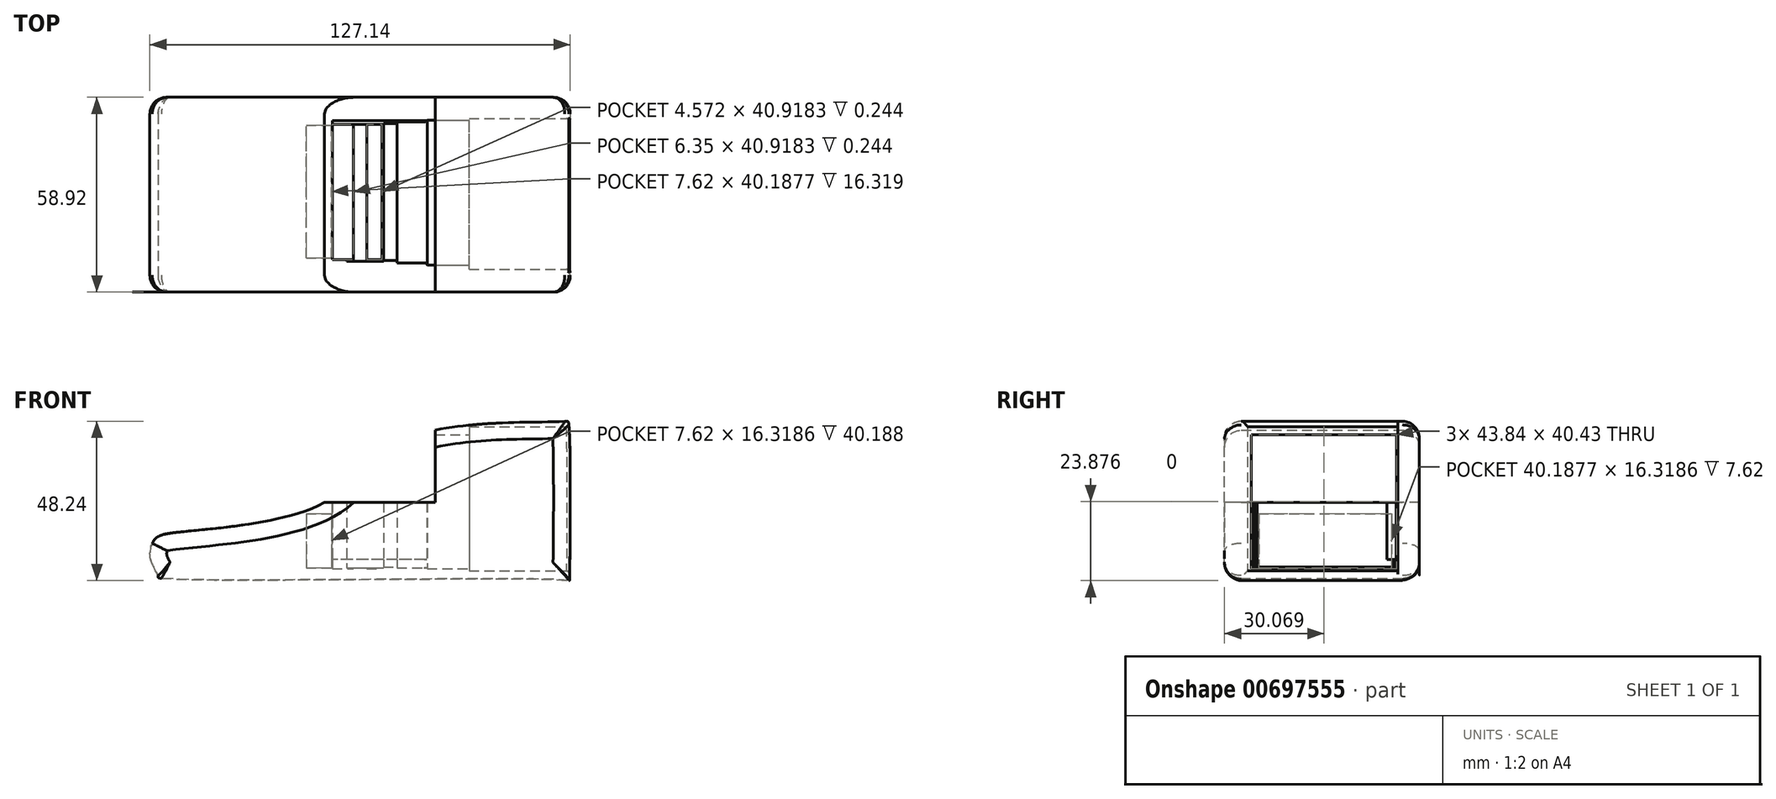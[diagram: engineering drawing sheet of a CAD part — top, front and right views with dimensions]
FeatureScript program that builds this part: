
annotation { "Feature Type Name" : "Feature", "Feature Type Description" : "" }
export const myFeature = defineFeature(function(context is Context, id is Id, definition is map)
    precondition{}
    {
        {
            var Q0;
            Q0=qCreatedBy(makeId("Front.planeOp"),FACE);
            var sketch = newSketch(context, id + "F0", { "sketchPlane" : qUnion([Q0])});
            skFitSpline(sketch, "E0", {"points": [v(-75, 0) * mm, v(-74, 5.82) * mm, v(-68.46, 8.09) * mm, v(-23.14, 16.9) * mm, v(3.56, 37.05) * mm, v(50.4, 41.83) * mm, v(51.4, 41.33) * mm, v(51.65, -6.27) * mm, v(51.4, -6.27) * mm, v(-72.5, -5.51) * mm, v(-72.74, -5) * mm, v(-75, 0) * mm]});
            skSolve(sketch);
        }
        {
            var Q0;
            Q0=makeQuery(id+"F0.imprint","IMPRINT",FACE,{"disambiguationData":[TD([[makeQuery(id+"F0.imprint","IMPRINT",EDGE,{"derivedFrom":sQuery(id+"F0.wireOp",EDGE,"E0")}),-1.0]])]});
            extrude(context, id + "F1", {"entities" : qUnion([Q0]), "endBound" : BoundingType.SYMMETRIC, "depth" : 58.93 * mm, "offsetDistance" : 25.4 * mm});
        }
        {
            var Q0;
            Q0=makeQuery(id+"F1.opExtrude","CAP_EDGE",EDGE,{"disambiguationData":[OSD([sQuery(id+"F0.wireOp",EDGE,"E0")])],"isStart":false});
            var Q1;
            Q1=makeQuery(id+"F1.opExtrude","CAP_EDGE",EDGE,{"disambiguationData":[OSD([sQuery(id+"F0.wireOp",EDGE,"E0")])],"isStart":true});
            fillet(context, id + "F2", {"entities" : qUnion([Q0, Q1]), "radius" : 5.08 * mm, "tangentPropagation" : true, "allowEdgeOverflow" : false});
        }
        {
            var Q0;
            Q0=qCreatedBy(makeId("Right.planeOp"),FACE);
            cPlane(context, id + "F3", {"entities" : qUnion([Q0]), "cplaneType" : CPlaneType.OFFSET, "offset" : 52.32 * mm, "width" : 152.4 * mm, "height" : 152.4 * mm});
        }
        {
            var Q0;
            Q0=qCreatedBy(id+"F3.planeOp",FACE);
            var sketch = newSketch(context, id + "F4", { "sketchPlane" : qUnion([Q0])});
            skLineSegment(sketch, "E1.bottom", {"start": v(-22.53, 40.19) * mm, "end": v(23.02, 40.19) * mm});
            skLineSegment(sketch, "E1.top", {"start": v(-22.53, -3.4) * mm, "end": v(23.02, -3.4) * mm});
            skLineSegment(sketch, "E1.left", {"start": v(-22.53, 40.19) * mm, "end": v(-22.53, -3.4) * mm});
            skLineSegment(sketch, "E1.right", {"start": v(23.02, 40.19) * mm, "end": v(23.02, -3.4) * mm});
            skSolve(sketch);
        }
        {
            var Q0;
            Q0=makeQuery(id+"F4.imprint","IMPRINT",FACE,{"disambiguationData":[TD([[makeQuery(id+"F4.imprint","IMPRINT",EDGE,{"derivedFrom":sQuery(id+"F4.wireOp",EDGE,"E1.bottom")}),-1.0]])]});
            extrude(context, id + "F5", {"entities" : qUnion([Q0]), "operationType" : NewBodyOperationType.REMOVE, "oppositeDirection" : true, "depth" : 30.99 * mm, "offsetDistance" : 25.4 * mm});
        }
        {
            var Q0;
            Q0=qCreatedBy(makeId("Right.planeOp"),FACE);
            cPlane(context, id + "F6", {"entities" : qUnion([Q0]), "cplaneType" : CPlaneType.OFFSET, "offset" : 21.34 * mm, "width" : 152.4 * mm, "height" : 152.4 * mm});
        }
        {
            var Q0;
            Q0=qCreatedBy(id+"F6.planeOp",FACE);
            var sketch = newSketch(context, id + "F7", { "sketchPlane" : qUnion([Q0])});
            skLineSegment(sketch, "E2.bottom", {"start": v(-21.31, 37.75) * mm, "end": v(22.53, 37.75) * mm});
            skLineSegment(sketch, "E2.top", {"start": v(-21.31, -2.68) * mm, "end": v(22.53, -2.68) * mm});
            skLineSegment(sketch, "E2.left", {"start": v(-21.31, 37.75) * mm, "end": v(-21.31, -2.68) * mm});
            skLineSegment(sketch, "E2.right", {"start": v(22.53, 37.75) * mm, "end": v(22.53, -2.68) * mm});
            skSolve(sketch);
        }
        {
            var Q0;
            Q0=makeQuery(id+"F7.imprint","IMPRINT",FACE,{"disambiguationData":[TD([[makeQuery(id+"F7.imprint","IMPRINT",EDGE,{"derivedFrom":sQuery(id+"F7.wireOp",EDGE,"E2.bottom")}),-1.0]])]});
            extrude(context, id + "F8", {"entities" : qUnion([Q0]), "operationType" : NewBodyOperationType.REMOVE, "oppositeDirection" : true, "depth" : 12.7 * mm, "offsetDistance" : 25.4 * mm});
        }
        {
            var Q0;
            Q0=qCreatedBy(makeId("Right.planeOp"),FACE);
            cPlane(context, id + "F9", {"entities" : qUnion([Q0]), "cplaneType" : CPlaneType.OFFSET, "offset" : 11.18 * mm, "width" : 152.4 * mm, "height" : 152.4 * mm});
        }
        {
            var Q0;
            Q0=qCreatedBy(id+"F9.planeOp",FACE);
            var sketch = newSketch(context, id + "F10", { "sketchPlane" : qUnion([Q0])});
            skLineSegment(sketch, "E3.bottom", {"start": v(-20.58, 34.59) * mm, "end": v(22.04, 34.59) * mm});
            skLineSegment(sketch, "E3.top", {"start": v(-20.58, -2.44) * mm, "end": v(22.04, -2.44) * mm});
            skLineSegment(sketch, "E3.left", {"start": v(-20.58, 34.59) * mm, "end": v(-20.58, -2.44) * mm});
            skLineSegment(sketch, "E3.right", {"start": v(22.04, 34.59) * mm, "end": v(22.04, -2.44) * mm});
            skSolve(sketch);
        }
        {
            var Q0;
            Q0=makeQuery(id+"F10.imprint","IMPRINT",FACE,{"disambiguationData":[TD([[makeQuery(id+"F10.imprint","IMPRINT",EDGE,{"derivedFrom":sQuery(id+"F10.wireOp",EDGE,"E3.bottom")}),-1.0]])]});
            extrude(context, id + "F11", {"entities" : qUnion([Q0]), "operationType" : NewBodyOperationType.REMOVE, "oppositeDirection" : true, "depth" : 11.68 * mm, "offsetDistance" : 25.4 * mm});
        }
        {
            var Q0;
            Q0=qCreatedBy(makeId("Right.planeOp"),FACE);
            var sketch = newSketch(context, id + "F12", { "sketchPlane" : qUnion([Q0])});
            skLineSegment(sketch, "E4.bottom", {"start": v(-19.85, 31.42) * mm, "end": v(21.56, 31.42) * mm});
            skLineSegment(sketch, "E4.top", {"start": v(-19.85, -2.2) * mm, "end": v(21.56, -2.2) * mm});
            skLineSegment(sketch, "E4.left", {"start": v(-19.85, 31.42) * mm, "end": v(-19.85, -2.2) * mm});
            skLineSegment(sketch, "E4.right", {"start": v(21.56, 31.42) * mm, "end": v(21.56, -2.2) * mm});
            skSolve(sketch);
        }
        {
            var Q0;
            Q0=makeQuery(id+"F12.imprint","IMPRINT",FACE,{"disambiguationData":[TD([[makeQuery(id+"F12.imprint","IMPRINT",EDGE,{"derivedFrom":sQuery(id+"F12.wireOp",EDGE,"E4.bottom")}),-1.0]])]});
            extrude(context, id + "F13", {"entities" : qUnion([Q0]), "operationType" : NewBodyOperationType.REMOVE, "oppositeDirection" : true, "depth" : 4.57 * mm, "offsetDistance" : 25.4 * mm});
        }
        {
            var Q0;
            Q0=qCreatedBy(makeId("Right.planeOp"),FACE);
            cPlane(context, id + "F14", {"entities" : qUnion([Q0]), "cplaneType" : CPlaneType.OFFSET, "offset" : 5.08 * mm, "oppositeDirection" : true, "width" : 152.4 * mm, "height" : 152.4 * mm});
        }
        {
            var Q0;
            Q0=qCreatedBy(id+"F14.planeOp",FACE);
            var sketch = newSketch(context, id + "F15", { "sketchPlane" : qUnion([Q0])});
            skLineSegment(sketch, "E5.bottom", {"start": v(-19.6, 26.55) * mm, "end": v(21.31, 26.55) * mm});
            skLineSegment(sketch, "E5.top", {"start": v(-19.6, -2.68) * mm, "end": v(21.31, -2.68) * mm});
            skLineSegment(sketch, "E5.left", {"start": v(-19.6, 26.55) * mm, "end": v(-19.6, -2.68) * mm});
            skLineSegment(sketch, "E5.right", {"start": v(21.31, 26.55) * mm, "end": v(21.31, -2.68) * mm});
            skSolve(sketch);
        }
        {
            var Q0;
            Q0 = qSketchRegion(id + "F15", true);
            extrude(context, id + "F16", {"entities" : qUnion([Q0]), "operationType" : NewBodyOperationType.REMOVE, "oppositeDirection" : true, "depth" : 4.57 * mm, "offsetDistance" : 25.4 * mm});
        }
        {
            var Q0;
            Q0=qCreatedBy(id+"F14.planeOp",FACE);
            cPlane(context, id + "F17", {"entities" : qUnion([Q0]), "cplaneType" : CPlaneType.OFFSET, "offset" : 5.08 * mm, "oppositeDirection" : true, "width" : 152.4 * mm, "height" : 152.4 * mm});
        }
        {
            var Q0;
            Q0=qCreatedBy(id+"F17.planeOp",FACE);
            var sketch = newSketch(context, id + "F18", { "sketchPlane" : qUnion([Q0])});
            skLineSegment(sketch, "E6.bottom", {"start": v(-20.1, 24.11) * mm, "end": v(21.31, 24.11) * mm});
            skLineSegment(sketch, "E6.top", {"start": v(-20.1, -2.44) * mm, "end": v(21.31, -2.44) * mm});
            skLineSegment(sketch, "E6.left", {"start": v(-20.1, 24.11) * mm, "end": v(-20.1, -2.44) * mm});
            skLineSegment(sketch, "E6.right", {"start": v(21.31, 24.11) * mm, "end": v(21.31, -2.44) * mm});
            skSolve(sketch);
        }
        {
            var Q0;
            Q0 = qSketchRegion(id + "F18", true);
            extrude(context, id + "F19", {"entities" : qUnion([Q0]), "operationType" : NewBodyOperationType.REMOVE, "oppositeDirection" : true, "depth" : 2.8 * mm, "offsetDistance" : 25.4 * mm});
        }
        {
            var Q0;
            Q0=qCreatedBy(id+"F17.planeOp",FACE);
            cPlane(context, id + "F20", {"entities" : qUnion([Q0]), "cplaneType" : CPlaneType.OFFSET, "offset" : 3.56 * mm, "oppositeDirection" : true, "width" : 152.4 * mm, "height" : 152.4 * mm});
        }
        {
            var Q0;
            Q0=qCreatedBy(id+"F20.planeOp",FACE);
            var sketch = newSketch(context, id + "F21", { "sketchPlane" : qUnion([Q0])});
            skLineSegment(sketch, "E7.bottom", {"start": v(-19.6, 18.02) * mm, "end": v(21.31, 18.02) * mm});
            skLineSegment(sketch, "E7.top", {"start": v(-19.6, -2.68) * mm, "end": v(21.31, -2.68) * mm});
            skLineSegment(sketch, "E7.left", {"start": v(-19.6, 18.02) * mm, "end": v(-19.6, -2.68) * mm});
            skLineSegment(sketch, "E7.right", {"start": v(21.31, 18.02) * mm, "end": v(21.31, -2.68) * mm});
            skSolve(sketch);
        }
        {
            var Q0;
            Q0 = qSketchRegion(id + "F21", true);
            extrude(context, id + "F22", {"entities" : qUnion([Q0]), "operationType" : NewBodyOperationType.REMOVE, "oppositeDirection" : true, "depth" : 6.35 * mm, "offsetDistance" : 25.4 * mm});
        }
        {
            var Q0;
            Q0=qCreatedBy(id+"F20.planeOp",FACE);
            cPlane(context, id + "F23", {"entities" : qUnion([Q0]), "cplaneType" : CPlaneType.OFFSET, "offset" : 6.6 * mm, "oppositeDirection" : true, "width" : 152.4 * mm, "height" : 152.4 * mm});
        }
        {
            var Q0;
            Q0=qCreatedBy(id+"F23.planeOp",FACE);
            var sketch = newSketch(context, id + "F24", { "sketchPlane" : qUnion([Q0])});
            skLineSegment(sketch, "E8.bottom", {"start": v(-19.12, 13.88) * mm, "end": v(21.07, 13.88) * mm});
            skLineSegment(sketch, "E8.top", {"start": v(-19.12, -2.44) * mm, "end": v(21.07, -2.44) * mm});
            skLineSegment(sketch, "E8.left", {"start": v(-19.12, 13.88) * mm, "end": v(-19.12, -2.44) * mm});
            skLineSegment(sketch, "E8.right", {"start": v(21.07, 13.88) * mm, "end": v(21.07, -2.44) * mm});
            skSolve(sketch);
        }
        {
            var Q0;
            Q0 = qSketchRegion(id + "F24", true);
            extrude(context, id + "F25", {"entities" : qUnion([Q0]), "operationType" : NewBodyOperationType.REMOVE, "oppositeDirection" : true, "depth" : 7.62 * mm, "offsetDistance" : 25.4 * mm});
        }
        {
            var Q0;
            Q0=makeQuery(id+"F5.boolean.opBoolean","INTERSECT",EDGE,{"derivedFrom":[makeQuery(id+"F1.opExtrude","SWEPT_FACE",FACE,{"disambiguationData":[OSD([sQuery(id+"F0.wireOp",EDGE,"E0")])]}),makeQuery(id+"F5.opExtrude","SWEPT_FACE",FACE,{"disambiguationData":[OSD([sQuery(id+"F4.wireOp",EDGE,"E1.bottom")])]})]});
            var Q1;
            Q1=makeQuery(id+"F8.boolean.opBoolean","COPY",EDGE,{"derivedFrom":makeQuery(id+"F8.opExtrude","CAP_EDGE",EDGE,{"disambiguationData":[OSD([sQuery(id+"F7.wireOp",EDGE,"E2.bottom")])],"isStart":true})});
            var Q2;
            Q2=makeQuery(id+"F11.boolean.opBoolean","INTERSECT",EDGE,{"derivedFrom":[makeQuery(id+"F8.boolean.opBoolean","COPY",FACE,{"derivedFrom":makeQuery(id+"F8.opExtrude","CAP_FACE",FACE,{"disambiguationData":[OSD([sQuery(id+"F7.wireOp",EDGE,"E2.bottom"),sQuery(id+"F7.wireOp",EDGE,"E2.top"),sQuery(id+"F7.wireOp",EDGE,"E2.left"),sQuery(id+"F7.wireOp",EDGE,"E2.right")])],"isStart":false})}),makeQuery(id+"F11.opExtrude","SWEPT_FACE",FACE,{"disambiguationData":[OSD([sQuery(id+"F10.wireOp",EDGE,"E3.bottom")])]})]});
            var Q3;
            Q3=makeQuery(id+"F13.boolean.opBoolean","INTERSECT",EDGE,{"derivedFrom":[makeQuery(id+"F11.boolean.opBoolean","COPY",FACE,{"derivedFrom":makeQuery(id+"F11.opExtrude","CAP_FACE",FACE,{"disambiguationData":[OSD([sQuery(id+"F10.wireOp",EDGE,"E3.bottom"),sQuery(id+"F10.wireOp",EDGE,"E3.top"),sQuery(id+"F10.wireOp",EDGE,"E3.left"),sQuery(id+"F10.wireOp",EDGE,"E3.right")])],"isStart":false})}),makeQuery(id+"F13.opExtrude","SWEPT_FACE",FACE,{"disambiguationData":[OSD([sQuery(id+"F12.wireOp",EDGE,"E4.bottom")])]})]});
            var Q4;
            Q4=makeQuery(id+"F11.boolean.opBoolean","INTERSECT",EDGE,{"derivedFrom":[makeQuery(id+"F8.boolean.opBoolean","COPY",FACE,{"derivedFrom":makeQuery(id+"F8.opExtrude","CAP_FACE",FACE,{"disambiguationData":[OSD([sQuery(id+"F7.wireOp",EDGE,"E2.bottom"),sQuery(id+"F7.wireOp",EDGE,"E2.top"),sQuery(id+"F7.wireOp",EDGE,"E2.left"),sQuery(id+"F7.wireOp",EDGE,"E2.right")])],"isStart":false})}),makeQuery(id+"F11.opExtrude","SWEPT_FACE",FACE,{"disambiguationData":[OSD([sQuery(id+"F10.wireOp",EDGE,"E3.left")])]})]});
            var Q5;
            Q5=makeQuery(id+"F5.boolean.opBoolean","INTERSECT",EDGE,{"derivedFrom":[makeQuery(id+"F1.opExtrude","SWEPT_FACE",FACE,{"disambiguationData":[OSD([sQuery(id+"F0.wireOp",EDGE,"E0")])]}),makeQuery(id+"F5.opExtrude","SWEPT_FACE",FACE,{"disambiguationData":[OSD([sQuery(id+"F4.wireOp",EDGE,"E1.left")])]})]});
            var Q6;
            Q6=makeQuery(id+"F5.boolean.opBoolean","INTERSECT",EDGE,{"derivedFrom":[makeQuery(id+"F1.opExtrude","SWEPT_FACE",FACE,{"disambiguationData":[OSD([sQuery(id+"F0.wireOp",EDGE,"E0")])]}),makeQuery(id+"F5.opExtrude","SWEPT_FACE",FACE,{"disambiguationData":[OSD([sQuery(id+"F4.wireOp",EDGE,"E1.top")])]})]});
            var Q7;
            Q7=makeQuery(id+"F8.boolean.opBoolean","COPY",EDGE,{"derivedFrom":makeQuery(id+"F8.opExtrude","CAP_EDGE",EDGE,{"disambiguationData":[OSD([sQuery(id+"F7.wireOp",EDGE,"E2.right")])],"isStart":true})});
            var Q8;
            Q8=makeQuery(id+"F11.boolean.opBoolean","INTERSECT",EDGE,{"derivedFrom":[makeQuery(id+"F8.boolean.opBoolean","COPY",FACE,{"derivedFrom":makeQuery(id+"F8.opExtrude","CAP_FACE",FACE,{"disambiguationData":[OSD([sQuery(id+"F7.wireOp",EDGE,"E2.bottom"),sQuery(id+"F7.wireOp",EDGE,"E2.top"),sQuery(id+"F7.wireOp",EDGE,"E2.left"),sQuery(id+"F7.wireOp",EDGE,"E2.right")])],"isStart":false})}),makeQuery(id+"F11.opExtrude","SWEPT_FACE",FACE,{"disambiguationData":[OSD([sQuery(id+"F10.wireOp",EDGE,"E3.right")])]})]});
            var Q9;
            Q9=makeQuery(id+"F8.boolean.opBoolean","COPY",EDGE,{"derivedFrom":makeQuery(id+"F8.opExtrude","CAP_EDGE",EDGE,{"disambiguationData":[OSD([sQuery(id+"F7.wireOp",EDGE,"E2.left")])],"isStart":true})});
            var Q10;
            Q10=makeQuery(id+"F8.boolean.opBoolean","COPY",EDGE,{"derivedFrom":makeQuery(id+"F8.opExtrude","CAP_EDGE",EDGE,{"disambiguationData":[OSD([sQuery(id+"F7.wireOp",EDGE,"E2.top")])],"isStart":true})});
            fillet(context, id + "F26", {"entities" : qUnion([Q0, Q1, Q2, Q3, Q4, Q5, Q6, Q7, Q8, Q9, Q10]), "radius" : 1.02 * mm, "tangentPropagation" : true, "allowEdgeOverflow" : false});
        }
        {
            var Q0;
            Q0=qCreatedBy(makeId("Front.planeOp"),FACE);
            var sketch = newSketch(context, id + "F27", { "sketchPlane" : qUnion([Q0])});
            skLineSegment(sketch, "E9.bottom", {"start": v(-24.78, 17.27) * mm, "end": v(11.03, 17.27) * mm});
            skLineSegment(sketch, "E9.top", {"start": v(-24.78, 42.36) * mm, "end": v(11.03, 42.36) * mm});
            skLineSegment(sketch, "E9.left", {"start": v(-24.78, 17.27) * mm, "end": v(-24.78, 42.36) * mm});
            skLineSegment(sketch, "E9.right", {"start": v(11.03, 17.27) * mm, "end": v(11.03, 42.36) * mm});
            skSolve(sketch);
        }
        {
            var Q0;
            Q0 = qSketchRegion(id + "F27", true);
            extrude(context, id + "F28", {"entities" : qUnion([Q0]), "operationType" : NewBodyOperationType.REMOVE, "endBound" : BoundingType.SYMMETRIC, "oppositeDirection" : true, "depth" : 68.07 * mm, "offsetDistance" : 25.4 * mm});
        }
        {
            var Q0;
            Q0=makeQuery(id+"F18.imprint","IMPRINT",FACE,{"disambiguationData":[TD([[makeQuery(id+"F18.imprint","IMPRINT",EDGE,{"derivedFrom":sQuery(id+"F18.wireOp",EDGE,"E6.bottom")}),-1.0]])]});
            extrude(context, id + "F29", {"entities" : qUnion([Q0]), "operationType" : NewBodyOperationType.REMOVE, "endBound" : BoundingType.SYMMETRIC, "oppositeDirection" : true, "depth" : 11.18 * mm, "offsetDistance" : 25.4 * mm});
        }
        {
            var Q0;
            Q0=qCreatedBy(makeId("Top.planeOp"),FACE);
            cPlane(context, id + "F30", {"entities" : qUnion([Q0]), "cplaneType" : CPlaneType.OFFSET, "offset" : 17.53 * mm, "width" : 152.4 * mm, "height" : 152.4 * mm});
        }
        {
            var Q0;
            Q0=qCreatedBy(id+"F30.planeOp",FACE);
            var sketch = newSketch(context, id + "F31", { "sketchPlane" : qUnion([Q0])});
            skLineSegment(sketch, "E10.bottom", {"start": v(9.36, 22.4) * mm, "end": v(-20.08, 22.4) * mm});
            skLineSegment(sketch, "E10.top", {"start": v(9.36, 19.59) * mm, "end": v(-20.08, 19.59) * mm});
            skLineSegment(sketch, "E10.left", {"start": v(9.36, 22.4) * mm, "end": v(9.36, 19.59) * mm});
            skLineSegment(sketch, "E10.right", {"start": v(-20.08, 22.4) * mm, "end": v(-20.08, 19.59) * mm});
            skSolve(sketch);
        }
        {
            var Q0;
            Q0 = qSketchRegion(id + "F31", true);
            extrude(context, id + "F32", {"entities" : qUnion([Q0]), "operationType" : NewBodyOperationType.REMOVE, "oppositeDirection" : true, "depth" : 17.53 * mm, "offsetDistance" : 25.4 * mm});
        }
    });
